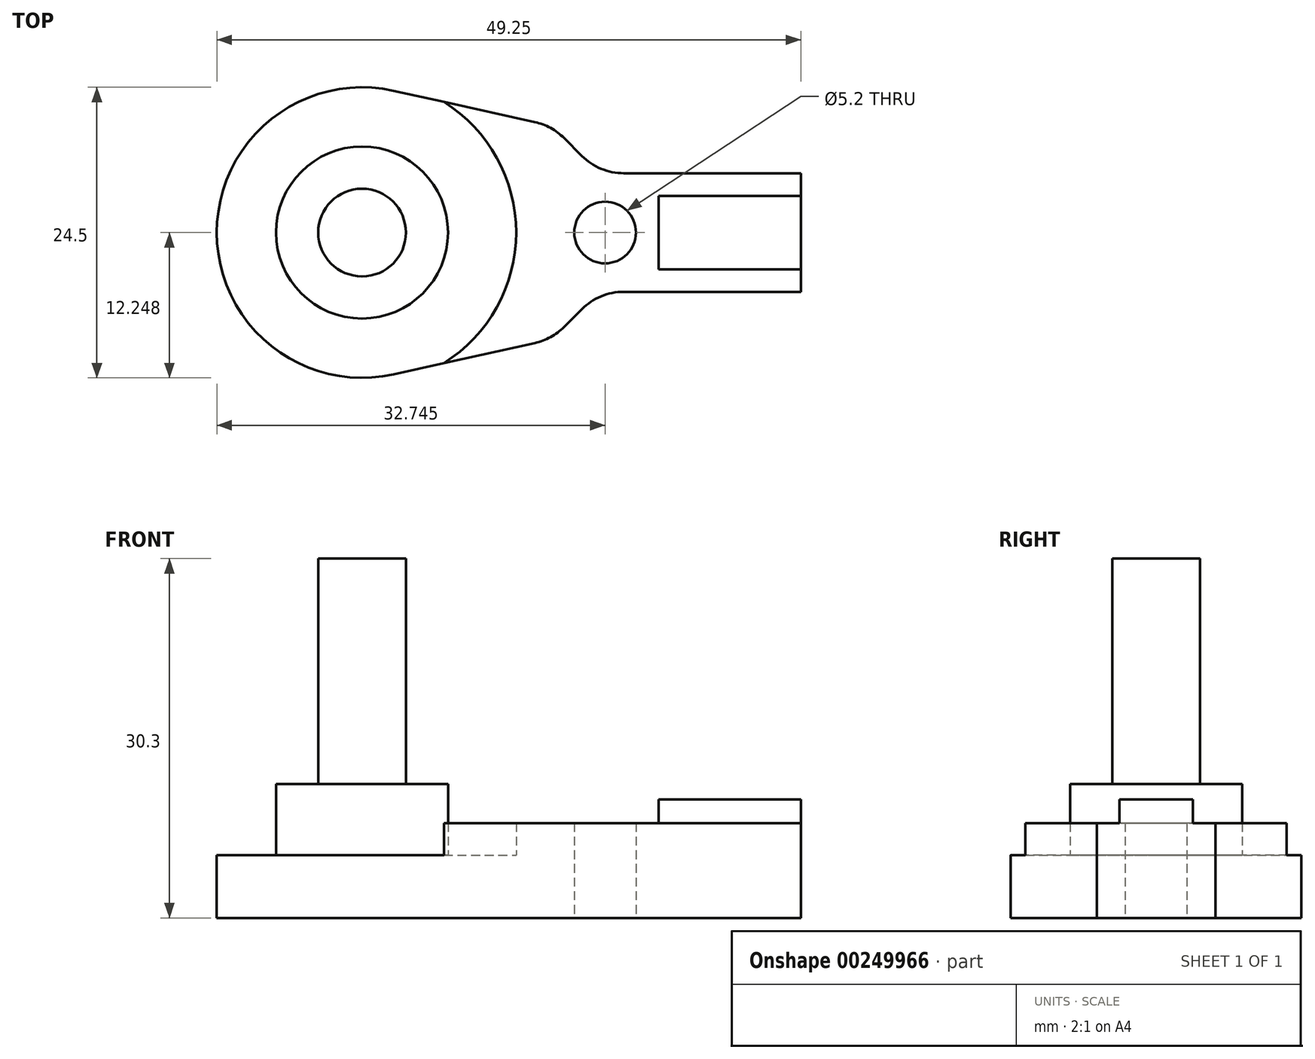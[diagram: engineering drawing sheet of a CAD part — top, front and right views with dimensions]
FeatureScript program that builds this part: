
annotation { "Feature Type Name" : "Feature", "Feature Type Description" : "" }
export const myFeature = defineFeature(function(context is Context, id is Id, definition is map)
    precondition{}
    {
        {
            var Q0;
            Q0=qCreatedBy(makeId("Top.planeOp"),FACE);
            var sketch = newSketch(context, id + "F0", { "sketchPlane" : qUnion([Q0])});
            skLineSegment(sketch, "E0", {"start": v(-16.35, -0.07) * mm, "end": v(-16.35, -5.07) * mm});
            skLineSegment(sketch, "E1", {"start": v(-16.35, -5.07) * mm, "end": v(-31.28, -5.07) * mm});
            skLineSegment(sketch, "E2", {"start": v(-34.82, -6.54) * mm, "end": v(-36.32, -8.04) * mm});
            skArc(sketch, "E3", {"start": v(-50.7, 11.89) * mm, "mid": v(-65.6, -0.07) * mm, "end": v(-50.7, -12.03) * mm});
            skPoint(sketch, "E3.centerSnap0", {"position": v(-16.35, -0.07) * mm});
            skLineSegment(sketch, "E4", {"start": v(-38.78, -9.39) * mm, "end": v(-50.7, -12.03) * mm});
            skLineSegment(sketch, "E5", {"start": v(-16.35, -0.07) * mm, "end": v(-76.81, -0.07) * mm, "construction": true});
            skPoint(sketch, "E6.orphan", {"position": v(-16.35, 4.93) * mm});
            skLineSegment(sketch, "E7.MirrorCS", {"start": v(-38.78, 9.24) * mm, "end": v(-50.7, 11.89) * mm});
            skLineSegment(sketch, "E8.MirrorCS", {"start": v(-16.35, -0.07) * mm, "end": v(-16.35, 4.93) * mm});
            skLineSegment(sketch, "E9.MirrorCS", {"start": v(-34.82, 6.4) * mm, "end": v(-36.32, 7.9) * mm});
            skLineSegment(sketch, "E10.MirrorCS", {"start": v(-16.35, 4.93) * mm, "end": v(-31.28, 4.93) * mm});
            skCircle(sketch, "E11", {"center": v(-32.85, -0.07) * mm, "radius": 2.6 * mm});
            skPoint(sketch, "E12.visualSharp", {"position": v(-37.35, 8.93) * mm});
            skArc(sketch, "E12.filletArc", {"start": v(-36.32, 7.9) * mm, "mid": v(-37.45, 8.75) * mm, "end": v(-38.78, 9.24) * mm});
            skPoint(sketch, "E13.visualSharp", {"position": v(-37.35, -9.07) * mm});
            skArc(sketch, "E13.filletArc", {"start": v(-38.78, -9.39) * mm, "mid": v(-37.45, -8.89) * mm, "end": v(-36.32, -8.04) * mm});
            skPoint(sketch, "E14.visualSharp", {"position": v(-33.35, -5.07) * mm});
            skArc(sketch, "E14.filletArc", {"start": v(-31.28, -5.07) * mm, "mid": v(-33.2, -5.45) * mm, "end": v(-34.82, -6.54) * mm});
            skPoint(sketch, "E15.visualSharp", {"position": v(-33.35, 4.93) * mm});
            skArc(sketch, "E15.filletArc", {"start": v(-34.82, 6.4) * mm, "mid": v(-33.2, 5.3) * mm, "end": v(-31.28, 4.93) * mm});
            skSolve(sketch);
        }
        {
            var Q0;
            Q0 = qSketchRegion(id + "F0", true);
            extrude(context, id + "F1", {"entities" : qUnion([Q0]), "depth" : 5.3 * mm});
        }
        {
            var Q0;
            Q0=makeQuery(id+"F1.opExtrude","CAP_FACE",FACE,{"disambiguationData":[OSD([sQuery(id+"F0.wireOp",EDGE,"E0"),sQuery(id+"F0.wireOp",EDGE,"E1"),sQuery(id+"F0.wireOp",EDGE,"E2"),sQuery(id+"F0.wireOp",EDGE,"E3"),sQuery(id+"F0.wireOp",EDGE,"E4"),sQuery(id+"F0.wireOp",EDGE,"E7.MirrorCS"),sQuery(id+"F0.wireOp",EDGE,"E8.MirrorCS"),sQuery(id+"F0.wireOp",EDGE,"E9.MirrorCS"),sQuery(id+"F0.wireOp",EDGE,"E10.MirrorCS"),sQuery(id+"F0.wireOp",EDGE,"E11"),sQuery(id+"F0.wireOp",EDGE,"E12.filletArc"),sQuery(id+"F0.wireOp",EDGE,"E13.filletArc"),sQuery(id+"F0.wireOp",EDGE,"E14.filletArc"),sQuery(id+"F0.wireOp",EDGE,"E15.filletArc")])],"isStart":false});
            var sketch = newSketch(context, id + "F2", { "sketchPlane" : qUnion([Q0])});
            skCircle(sketch, "E16", {"center": v(-53.35, -0.07) * mm, "radius": 7.25 * mm});
            skArc(sketch, "E17", {"start": v(-46.45, -11.09) * mm, "mid": v(-40.35, -0.07) * mm, "end": v(-46.45, 10.95) * mm});
            skLineSegment(sketch, "E18", {"start": v(-46.45, 10.95) * mm, "end": v(-38.78, 9.24) * mm});
            skLineSegment(sketch, "E19", {"start": v(-16.35, 4.93) * mm, "end": v(-16.35, -0.07) * mm});
            skLineSegment(sketch, "E20", {"start": v(-16.35, 4.93) * mm, "end": v(-31.28, 4.93) * mm});
            skLineSegment(sketch, "E21", {"start": v(-36.32, 7.9) * mm, "end": v(-34.82, 6.4) * mm});
            skLineSegment(sketch, "E22", {"start": v(-36.32, 7.9) * mm, "end": v(-36.32, 7.9) * mm});
            skPoint(sketch, "E23.orphan", {"position": v(-34.82, 8.37) * mm});
            skPoint(sketch, "E24.visualSharp", {"position": v(-37.35, 8.93) * mm});
            skArc(sketch, "E24.filletArc", {"start": v(-36.32, 7.9) * mm, "mid": v(-37.45, 8.75) * mm, "end": v(-38.78, 9.24) * mm});
            skPoint(sketch, "E25.visualSharp", {"position": v(-33.35, 4.93) * mm});
            skArc(sketch, "E25.filletArc", {"start": v(-34.82, 6.4) * mm, "mid": v(-33.2, 5.3) * mm, "end": v(-31.28, 4.93) * mm});
            skLineSegment(sketch, "E26", {"start": v(-16.35, -0.07) * mm, "end": v(-28.63, -0.07) * mm, "construction": true});
            skLineSegment(sketch, "E27.MirrorCS", {"start": v(-16.35, -5.07) * mm, "end": v(-16.35, -0.07) * mm});
            skLineSegment(sketch, "E28.MirrorCS", {"start": v(-46.45, -11.09) * mm, "end": v(-38.78, -9.39) * mm});
            skArc(sketch, "E29.MirrorCS", {"start": v(-36.32, -8.04) * mm, "mid": v(-37.45, -8.89) * mm, "end": v(-38.78, -9.39) * mm});
            skArc(sketch, "E30.MirrorCS", {"start": v(-34.82, -6.54) * mm, "mid": v(-33.2, -5.45) * mm, "end": v(-31.28, -5.07) * mm});
            skLineSegment(sketch, "E31.MirrorCS", {"start": v(-36.32, -8.04) * mm, "end": v(-34.82, -6.54) * mm});
            skLineSegment(sketch, "E32.MirrorCS", {"start": v(-16.35, -5.07) * mm, "end": v(-31.28, -5.07) * mm});
            skPoint(sketch, "E33.MirrorP", {"position": v(-34.82, -8.5) * mm});
            skPoint(sketch, "E34.MirrorP", {"position": v(-37.35, -9.07) * mm});
            skPoint(sketch, "E35.MirrorP", {"position": v(-33.35, -5.07) * mm});
            skCircle(sketch, "E36", {"center": v(-32.85, -0.07) * mm, "radius": 2.6 * mm});
            skSolve(sketch);
        }
        {
            var Q0;
            Q0=makeQuery(id+"F2.imprint","IMPRINT",FACE,{"disambiguationData":[TD([[makeQuery(id+"F2.imprint","IMPRINT",EDGE,{"derivedFrom":sQuery(id+"F2.wireOp",EDGE,"E16")}),1.0]])]});
            extrude(context, id + "F3", {"entities" : qUnion([Q0]), "operationType" : NewBodyOperationType.ADD, "depth" : 6 * mm});
        }
        {
            var Q0;
            Q0=makeQuery(id+"F2.imprint","IMPRINT",FACE,{"disambiguationData":[TD([[makeQuery(id+"F2.imprint","IMPRINT",EDGE,{"derivedFrom":sQuery(id+"F2.wireOp",EDGE,"E17")}),-1.0]])]});
            extrude(context, id + "F4", {"entities" : qUnion([Q0]), "operationType" : NewBodyOperationType.ADD, "depth" : 2.7 * mm});
        }
        {
            var Q0;
            Q0=makeQuery(id+"F4.opExtrude","CAP_FACE",FACE,{"disambiguationData":[OSD([sQuery(id+"F2.wireOp",EDGE,"E17"),sQuery(id+"F2.wireOp",EDGE,"E18"),sQuery(id+"F2.wireOp",EDGE,"E19"),sQuery(id+"F2.wireOp",EDGE,"E20"),sQuery(id+"F2.wireOp",EDGE,"E21"),sQuery(id+"F2.wireOp",EDGE,"E24.filletArc"),sQuery(id+"F2.wireOp",EDGE,"E25.filletArc"),sQuery(id+"F2.wireOp",EDGE,"E27.MirrorCS"),sQuery(id+"F2.wireOp",EDGE,"E28.MirrorCS"),sQuery(id+"F2.wireOp",EDGE,"E29.MirrorCS"),sQuery(id+"F2.wireOp",EDGE,"E30.MirrorCS"),sQuery(id+"F2.wireOp",EDGE,"E31.MirrorCS"),sQuery(id+"F2.wireOp",EDGE,"E32.MirrorCS"),sQuery(id+"F2.wireOp",EDGE,"E36")])],"isStart":false});
            var sketch = newSketch(context, id + "F5", { "sketchPlane" : qUnion([Q0])});
            skLineSegment(sketch, "E37.bottom", {"start": v(-16.35, 3.03) * mm, "end": v(-28.35, 3.03) * mm});
            skLineSegment(sketch, "E37.top", {"start": v(-16.35, -3.17) * mm, "end": v(-28.35, -3.17) * mm});
            skLineSegment(sketch, "E37.left", {"start": v(-16.35, 3.03) * mm, "end": v(-16.35, -3.17) * mm});
            skLineSegment(sketch, "E37.right", {"start": v(-28.35, 3.03) * mm, "end": v(-28.35, -3.17) * mm});
            skSolve(sketch);
        }
        {
            var Q0;
            Q0=makeQuery(id+"F5.imprint","IMPRINT",FACE,{"disambiguationData":[TD([[makeQuery(id+"F5.imprint","IMPRINT",EDGE,{"derivedFrom":sQuery(id+"F5.wireOp",EDGE,"E37.bottom")}),1.0]])]});
            extrude(context, id + "F6", {"entities" : qUnion([Q0]), "operationType" : NewBodyOperationType.ADD, "depth" : 2 * mm});
        }
        {
            var Q0;
            Q0=makeQuery(id+"F3.opExtrude","CAP_FACE",FACE,{"disambiguationData":[OSD([sQuery(id+"F2.wireOp",EDGE,"E16")])],"isStart":false});
            var sketch = newSketch(context, id + "F7", { "sketchPlane" : qUnion([Q0])});
            skCircle(sketch, "E38", {"center": v(-53.35, -0.07) * mm, "radius": 3.7 * mm});
            skSolve(sketch);
        }
        {
            var Q0;
            Q0 = qSketchRegion(id + "F7", true);
            extrude(context, id + "F8", {"entities" : qUnion([Q0]), "operationType" : NewBodyOperationType.ADD, "depth" : 19 * mm});
        }
    });
